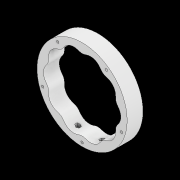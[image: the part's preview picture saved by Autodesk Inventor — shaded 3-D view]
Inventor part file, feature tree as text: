
AUTODESK INVENTOR PART (.ipt)
format: ipt  version: 2022.2 (Build 262287010, 287A)  size: 366,592 bytes
history: native  units: mm
features: sketch x11, extrude x10, other x3, pattern_circular x3, plane x1, hole x1, fillet x1
ambient origin geometry x8: Origin, YZ Plane, XZ Plane, XY Plane, X Axis, Y Axis, Z Axis, Center Point
bodies: Solid3 (feature_tree)
feature tree (30):
  other  "CrossSection1"
  sketch  "Sketch3"  dims[d59=66.75mm d61=0.0mm d62=3600.0mm]
  sketch  "Sketch1"  dims[d4=150.0mm d19=12.0mm]
  plane  "Work Plane1"
  sketch  "Sketch9"  dims[d91=23.65mm d93=60.0mm]
  extrude  "Extrusion7"  Depth=12.0mm
  sketch  "Sketch10"  dims[d94=30.0mm d95=200.000423mm]
  extrude  "Extrusion10"  Depth=3600.0mm TaperAngle=0.0deg
  pattern_circular  "Circular Pattern4"  Count=6  [1 undecoded]
  extrude  "Extrusion8"  Depth=200.000423mm
  extrude  "Extrusion9"  Depth=26.0mm TaperAngle=0.0deg
  pattern_circular  "Circular Pattern3"  [2 undecoded]
  extrude  "Extrusion3"  Depth=2.0mm TaperAngle=0.0deg
  hole  "Hole3"  [1 undecoded]
  pattern_circular  "Circular Pattern5"  [2 undecoded]
  sketch  "Sketch13"  dims[d102=29.0mm d103=0.0mm d104=2.0mm d105=0.0mm d106=3600.0mm d111=100.0mm d112=69.0mm d113=2.5mm d114=0.0mm d115=3.0mm d116=0.0mm d117=0.0mm d118=5.5mm d119=2.5mm d120=0.0mm d121=50.0mm d122=360.0deg d124=2.5mm d125=0.0mm d126=50.0mm d127=360.0deg d129=22.5mm d130=2.5mm d131=0.0mm d132=138.0mm d133=4.0mm d134=6.0mm d135=4.0mm d136=2.0mm d137=90.0deg d138=4.0mm d139=0.0mm d140=50.0mm d141=360.0deg d143=0.5mm d144=2.0mm d145=0.0mm d146=20.0mm d147=3.1416mm d148=3.141586mm d149=7.0mm d150=7.0mm d151=65.564mm d152=0.0mm d153=4.0mm d154=4.0mm d155=0.0mm d156=0.0mm]
  extrude  "Extrusion12"  Depth=2.0mm TaperAngle=0.0deg
  extrude  "Extrusion13"  Depth=2.0mm
  sketch  "Sketch4"  dims[d66=12.0mm]
  sketch  "Sketch5"  dims[d67=63.483mm]
  extrude  "Extrusion4"  TaperAngle=0.0deg  [1 undecoded]
  sketch  "Sketch7"  dims[d68=138.0mm]
  extrude  "Extrusion6"  Depth=2.0mm
  fillet  "Fillet1"  Radius=2.5mm
  extrude  "Extrusion11"  Depth=2.0mm TaperAngle=360.0deg
  other  "2D Equation Curve10"
  sketch  "Sketch8"  dims[d69=26.3mm d70=0.0mm]
  other  "2D Equation Curve11"
  sketch  "Sketch11"  dims[d96=23.65mm d97=26.0mm d98=0.0mm]
  sketch  "Sketch12"  dims[d99=156.0mm]
note: 7 required parameter values undecoded (feature->parameter linkage not recoverable at this tier; creation-order binding heuristic only, values carry confidence <= 0.55)
